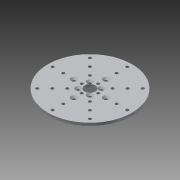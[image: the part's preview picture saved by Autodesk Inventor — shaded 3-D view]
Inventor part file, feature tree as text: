
AUTODESK INVENTOR PART (.ipt)
format: ipt  version: 2015 (Build 190159000, 159)  size: 284,160 bytes
history: native  units: in
note: dims shown in document units (in); Inventor stores cm internally (conversion verified against a paired STEP export)
features: hole x2, sketch x2, other x1, imported_body x1
ambient origin geometry x8: Origin, YZ Plane, XZ Plane, XY Plane, X Axis, Y Axis, Z Axis, Center Point
bodies: Solid1 (feature_tree)
feature tree (6):
  other  "User Library-585438.sat1"
  hole  "Hole1"  [1 undecoded]
  hole  "Hole2"  [1 undecoded]
  imported_body  "Base1"
  sketch  "Sketch2"  dims[d4=0.1406in d5=0.144in]
  sketch  "Sketch3"  dims[d6=0.1406in d7=0.1406in d8=0.144in d9=0.1406in d10=0.1406in d11=0.1406in d12=0.1406in d13=0.141in d14=0.75in d15=0.375in d16=0.25in d17=0.5635in d18=1.0in d19=0.8108in d20=0.144in d21=0.144in d22=0.144in d23=0.144in d24=0.144in d25=0.144in d27=0.144in d28=0.144in d29=0.145in d30=0.75in d31=0.375in d32=0.25in d33=0.5635in d34=1.0in d35=0.8108in]
note: 2 required parameter values undecoded (feature->parameter linkage not recoverable at this tier; creation-order binding heuristic only, values carry confidence <= 0.55)
